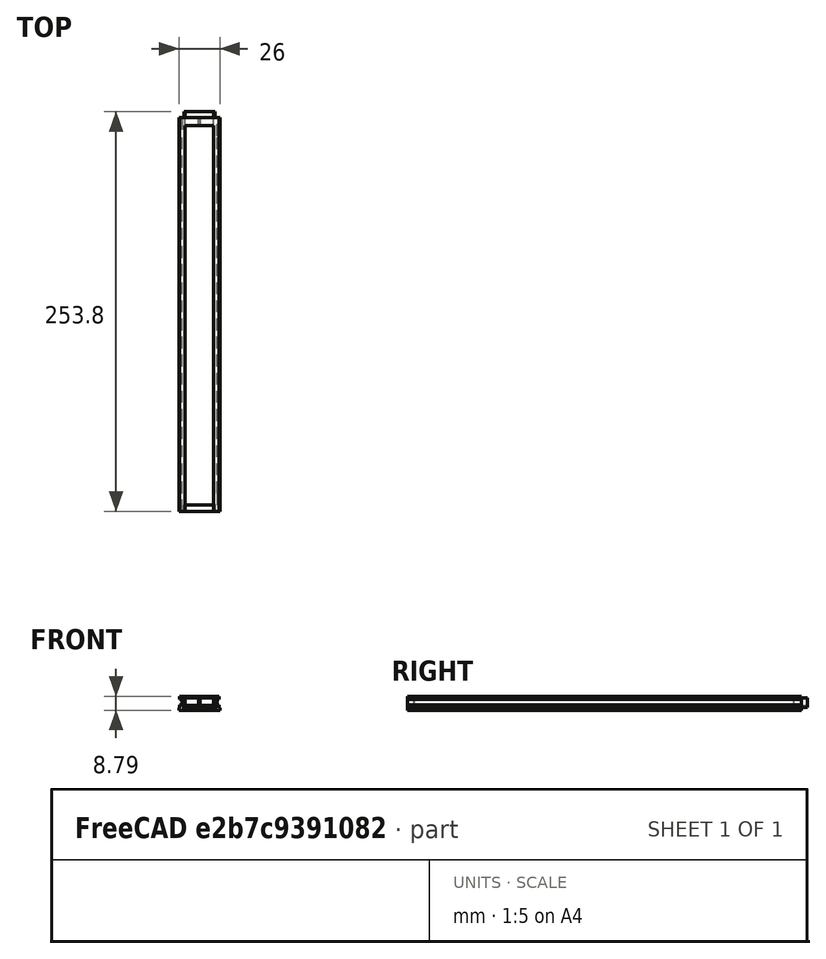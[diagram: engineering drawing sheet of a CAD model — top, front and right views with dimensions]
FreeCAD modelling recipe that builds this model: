
FCSTD DOCUMENT  (FreeCAD 0.18.3R)
Label: lamp.rail.25cm
License: All rights reserved
LicenseURL: http://en.wikipedia.org/wiki/All_rights_reserved
objects: Part::Feature×4, Part::Extrusion×3, Part::MultiFuse×3
note: 10 computed .brp shape members not serialized (recipe doc carries the construction recipe); baked Part::Feature solids carry a one-line shape summary decoded from their .brp

FEATURE [Part::Feature] Cut047_solid001  label="Cut047 (Solid)001"
  Placement = pos=(36.1596,254.509,-3.59e-14) rot=(0,0,1;0rad)
  shape: bbox 26 x 15.3 x 8.799 mm, 30 faces (baked)
FEATURE [Part::Feature] Cut037_solid001001  label="Cut037 (Solid)002"
  Placement = pos=(36.1596,-5.32723,-2.2e-15) rot=(0,0,1;0rad)
  shape: bbox 26 x 11.5 x 8.799 mm, 28 faces (baked)
FEATURE [Part::Feature] Face
  Placement = pos=(36.1596,-5.32723,-2e-15) rot=(0,0,1;0rad)
  shape: bbox 26 x 5.243e-07 x 8.799 mm, 1 faces, 0 solids (baked)
FEATURE [Part::Extrusion] Extrusion
  Base = -> Face
  Dir = (7.72e-14,227,-5.45e-14)
  DirMode = 0
  FaceMakerClass = Part::FaceMakerBullseye
  LengthFwd = 0
  LengthRev = 0
  Solid = true
  Symmetric = false
FEATURE [Part::MultiFuse] Fusion
  Shapes = -> [Cut047_solid001,Cut037_solid001001,Extrusion]
FEATURE [Part::Extrusion] Extrusion038
  Dir = (8.3e-15,-2.72e-14,-4.79945)
  DirMode = 0
  FaceMakerClass = Part::FaceMakerBullseye
  LengthFwd = 0
  LengthRev = 0
  Solid = true
  Symmetric = false
FEATURE [Part::Extrusion] Extrusion039
  Dir = (18,0,0)
  DirMode = 0
  FaceMakerClass = Part::FaceMakerBullseye
  LengthFwd = 0
  LengthRev = 0
  Solid = true
  Symmetric = false
FEATURE [Part::MultiFuse] Fusion001
  Placement = pos=(24.4812,182.869,-4) rot=(0,0,1;0rad)
  Shapes = -> [Extrusion038,Extrusion039]
FEATURE [Part::MultiFuse] Fusion002
  Shapes = -> [Fusion,Fusion001]
FEATURE [Part::Feature] Fusion002_solid001  label="Fusion002 (Solid)001"
  Placement = pos=(-50.9745,1.8698,11.7995) rot=(0,0,1;0rad)
  shape: bbox 26 x 253.8 x 8.799 mm, 40 faces (baked)
